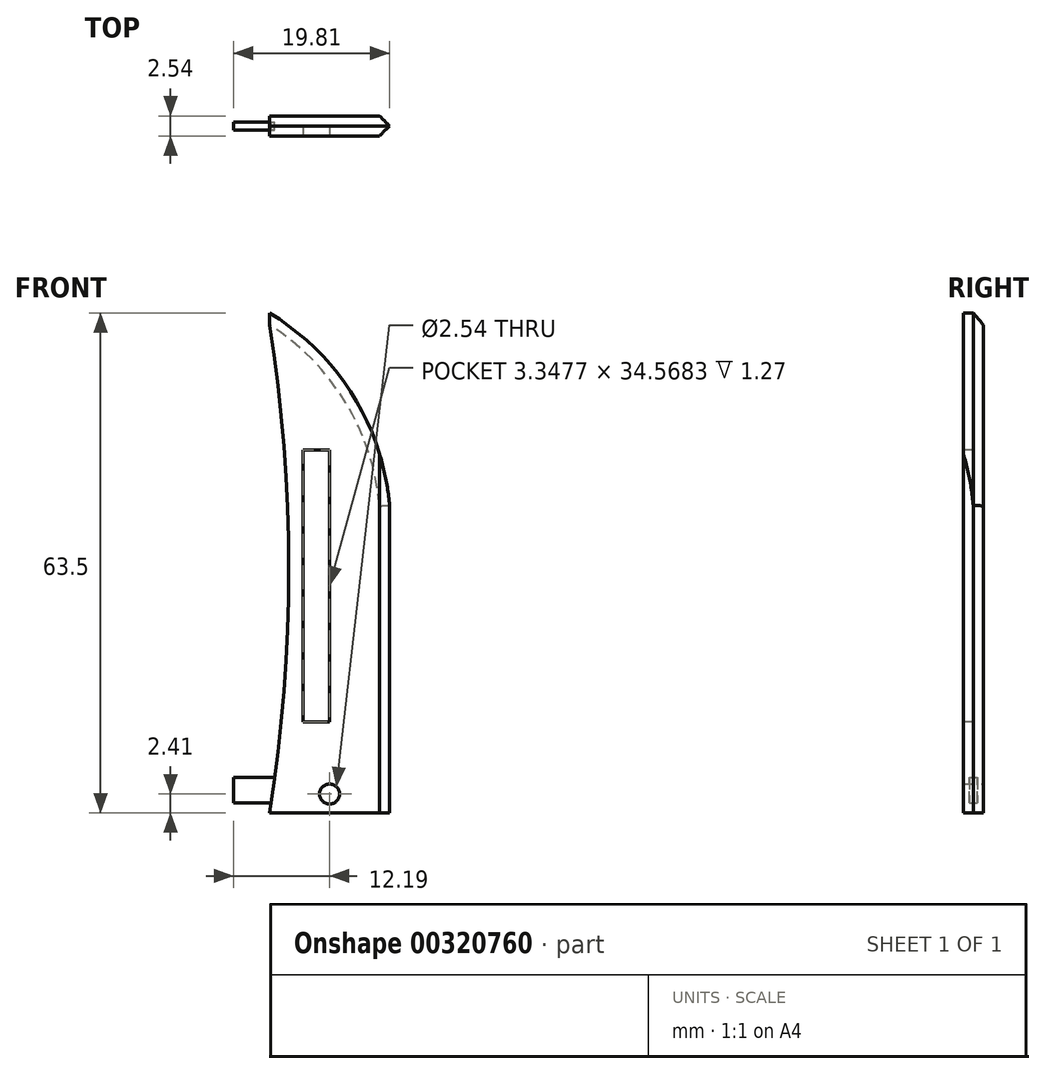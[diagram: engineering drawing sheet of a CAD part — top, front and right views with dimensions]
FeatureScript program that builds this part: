
annotation { "Feature Type Name" : "Feature", "Feature Type Description" : "" }
export const myFeature = defineFeature(function(context is Context, id is Id, definition is map)
    precondition{}
    {
        {
            var Q0;
            Q0=qCreatedBy(makeId("Front.planeOp"),FACE);
            var sketch = newSketch(context, id + "F0", { "sketchPlane" : qUnion([Q0])});
            skLineSegment(sketch, "E0", {"start": v(-7.62, 0) * mm, "end": v(-7.62, 63.5) * mm});
            skLineSegment(sketch, "E1", {"start": v(-7.62, 63.5) * mm, "end": v(7.62, 54.34) * mm});
            skLineSegment(sketch, "E2", {"start": v(7.62, 54.34) * mm, "end": v(7.62, 0) * mm});
            skLineSegment(sketch, "E3", {"start": v(7.62, 0) * mm, "end": v(-7.62, 0) * mm});
            skSolve(sketch);
        }
        {
            var Q0;
            Q0 = qSketchRegion(id + "F0", true);
            extrude(context, id + "F1", {"entities" : qUnion([Q0]), "endBound" : BoundingType.SYMMETRIC, "depth" : 2.54 * mm});
        }
        {
            var Q0;
            Q0=makeQuery(id+"F1.opExtrude","CAP_FACE",FACE,{"disambiguationData":[OSD([sQuery(id+"F0.wireOp",EDGE,"E0"),sQuery(id+"F0.wireOp",EDGE,"E1"),sQuery(id+"F0.wireOp",EDGE,"E2"),sQuery(id+"F0.wireOp",EDGE,"E3")])],"isStart":false});
            var sketch = newSketch(context, id + "F2", { "sketchPlane" : qUnion([Q0])});
            skArc(sketch, "E4", {"start": v(7.62, 39.07) * mm, "mid": v(2.94, 53.12) * mm, "end": v(-7.62, 63.5) * mm});
            skLineSegment(sketch, "E5", {"start": v(7.62, 39.07) * mm, "end": v(7.62, 63.5) * mm});
            skLineSegment(sketch, "E6", {"start": v(7.62, 63.5) * mm, "end": v(-7.62, 63.5) * mm});
            skSolve(sketch);
        }
        {
            var Q0;
            Q0 = qSketchRegion(id + "F2", true);
            extrude(context, id + "F3", {"entities" : qUnion([Q0]), "operationType" : NewBodyOperationType.REMOVE, "oppositeDirection" : true, "depth" : 25.4 * mm});
        }
        {
            var Q0;
            Q0=makeQuery(id+"F1.opExtrude","CAP_EDGE",EDGE,{"disambiguationData":[OSD([sQuery(id+"F0.wireOp",EDGE,"E2")])],"isStart":true});
            var Q1;
            Q1=makeQuery(id+"F3.boolean.opBoolean","INTERSECT",EDGE,{"derivedFrom":[makeQuery(id+"F1.opExtrude","CAP_FACE",FACE,{"disambiguationData":[OSD([sQuery(id+"F0.wireOp",EDGE,"E0"),sQuery(id+"F0.wireOp",EDGE,"E1"),sQuery(id+"F0.wireOp",EDGE,"E2"),sQuery(id+"F0.wireOp",EDGE,"E3")])],"isStart":true}),makeQuery(id+"F3.opExtrude","SWEPT_FACE",FACE,{"disambiguationData":[OSD([sQuery(id+"F2.wireOp",EDGE,"E4")])]})]});
            var Q2;
            Q2=makeQuery(id+"F1.opExtrude","CAP_EDGE",EDGE,{"disambiguationData":[OSD([sQuery(id+"F0.wireOp",EDGE,"E2")])],"isStart":false});
            var Q3;
            Q3=makeQuery(id+"F3.boolean.opBoolean","COPY",EDGE,{"derivedFrom":makeQuery(id+"F3.opExtrude","CAP_EDGE",EDGE,{"disambiguationData":[OSD([sQuery(id+"F2.wireOp",EDGE,"E4")])],"isStart":true})});
            chamfer(context, id + "F4", {"entities" : qUnion([Q0, Q1, Q2, Q3]), "width" : 1.27 * mm, "tangentPropagation" : true});
        }
        {
            var Q0;
            Q0=makeQuery(id+"F1.opExtrude","CAP_FACE",FACE,{"disambiguationData":[OSD([sQuery(id+"F0.wireOp",EDGE,"E0"),sQuery(id+"F0.wireOp",EDGE,"E1"),sQuery(id+"F0.wireOp",EDGE,"E2"),sQuery(id+"F0.wireOp",EDGE,"E3")])],"isStart":true});
            var sketch = newSketch(context, id + "F5", { "sketchPlane" : qUnion([Q0])});
            skArc(sketch, "E7", {"start": v(7.62, 62) * mm, "mid": v(5.19, 31) * mm, "end": v(7.62, 0) * mm});
            skLineSegment(sketch, "E8", {"start": v(7.62, 62) * mm, "end": v(7.62, 0) * mm});
            skSolve(sketch);
        }
        {
            var Q0;
            Q0 = qSketchRegion(id + "F5", true);
            extrude(context, id + "F6", {"entities" : qUnion([Q0]), "operationType" : NewBodyOperationType.REMOVE, "oppositeDirection" : true, "depth" : 25.4 * mm});
        }
        {
            var Q0;
            Q0=makeQuery(id+"F1.opExtrude","CAP_FACE",FACE,{"disambiguationData":[OSD([sQuery(id+"F0.wireOp",EDGE,"E0"),sQuery(id+"F0.wireOp",EDGE,"E1"),sQuery(id+"F0.wireOp",EDGE,"E2"),sQuery(id+"F0.wireOp",EDGE,"E3")])],"isStart":true});
            var sketch = newSketch(context, id + "F7", { "sketchPlane" : qUnion([Q0])});
            skCircle(sketch, "E9", {"center": v(0, 2.4) * mm, "radius": 1.27 * mm});
            skSolve(sketch);
        }
        {
            var Q0;
            Q0 = qSketchRegion(id + "F7", true);
            extrude(context, id + "F8", {"entities" : qUnion([Q0]), "operationType" : NewBodyOperationType.REMOVE, "oppositeDirection" : true, "depth" : 25.4 * mm});
        }
        {
            var Q0;
            Q0=makeQuery(id+"F1.opExtrude","CAP_FACE",FACE,{"disambiguationData":[OSD([sQuery(id+"F0.wireOp",EDGE,"E0"),sQuery(id+"F0.wireOp",EDGE,"E1"),sQuery(id+"F0.wireOp",EDGE,"E2"),sQuery(id+"F0.wireOp",EDGE,"E3")])],"isStart":false});
            var sketch = newSketch(context, id + "F9", { "sketchPlane" : qUnion([Q0])});
            skLineSegment(sketch, "E10.bottom", {"start": v(-3.35, 46.12) * mm, "end": v(0, 46.12) * mm});
            skLineSegment(sketch, "E10.top", {"start": v(-3.35, 11.55) * mm, "end": v(0, 11.55) * mm});
            skLineSegment(sketch, "E10.left", {"start": v(-3.35, 46.12) * mm, "end": v(-3.35, 11.55) * mm});
            skLineSegment(sketch, "E10.right", {"start": v(0, 46.12) * mm, "end": v(0, 11.55) * mm});
            skSolve(sketch);
        }
        {
            var Q0;
            Q0 = qSketchRegion(id + "F9", true);
            extrude(context, id + "F10", {"entities" : qUnion([Q0]), "operationType" : NewBodyOperationType.REMOVE, "oppositeDirection" : true, "depth" : 1.27 * mm});
        }
        {
            var Q0;
            Q0=makeQuery(id+"F10.boolean.opBoolean","COPY",FACE,{"derivedFrom":makeQuery(id+"F10.opExtrude","CAP_FACE",FACE,{"disambiguationData":[OSD([sQuery(id+"F9.wireOp",EDGE,"E10.bottom"),sQuery(id+"F9.wireOp",EDGE,"E10.top"),sQuery(id+"F9.wireOp",EDGE,"E10.left"),sQuery(id+"F9.wireOp",EDGE,"E10.right")])],"isStart":false})});
            var sketch = newSketch(context, id + "F11", { "sketchPlane" : qUnion([Q0])});
            skSolve(sketch);
        }
        {
            var Q0;
            Q0=makeQuery(id+"F11.imprint","IMPRINT",FACE,{"disambiguationData":[TD([[makeQuery(id+"F11.imprint","IMPRINT",EDGE,{"derivedFrom":makeQuery(id+"F10.boolean.opBoolean","COPY",EDGE,{"derivedFrom":makeQuery(id+"F10.opExtrude","CAP_EDGE",EDGE,{"disambiguationData":[OSD([sQuery(id+"F9.wireOp",EDGE,"E10.bottom")])],"isStart":false})})}),-1.0]])]});
            extrude(context, id + "F12", {"entities" : qUnion([Q0]), "depth" : 1.27 * mm});
        }
        {
            var Q0;
            Q0 = qSketchRegion(id + "F9", true);
            extrude(context, id + "F13", {"entities" : qUnion([Q0]), "operationType" : NewBodyOperationType.REMOVE, "oppositeDirection" : true, "depth" : 1.27 * mm});
        }
        {
            var Q0;
            Q0=qCreatedBy(makeId("Right.planeOp"),FACE);
            var sketch = newSketch(context, id + "F14", { "sketchPlane" : qUnion([Q0])});
            skLineSegment(sketch, "E11", {"start": v(0.5, 1.25) * mm, "end": v(-0.5, 1.25) * mm});
            skLineSegment(sketch, "E12", {"start": v(-0.5, 1.25) * mm, "end": v(-0.5, 4.51) * mm});
            skLineSegment(sketch, "E13", {"start": v(-0.5, 4.51) * mm, "end": v(0.5, 4.51) * mm});
            skLineSegment(sketch, "E14", {"start": v(0.5, 4.51) * mm, "end": v(0.5, 1.25) * mm});
            skSolve(sketch);
        }
        {
            var Q0;
            Q0 = qSketchRegion(id + "F14", true);
            extrude(context, id + "F15", {"entities" : qUnion([Q0]), "operationType" : NewBodyOperationType.ADD, "oppositeDirection" : true, "depth" : 12.2 * mm});
        }
        {
            var Q0;
            Q0=qCreatedBy(makeId("Front.planeOp"),FACE);
            var sketch = newSketch(context, id + "F16", { "sketchPlane" : qUnion([Q0])});
            skCircle(sketch, "E15.0", {"center": v(0, 2.4) * mm, "radius": 1.27 * mm});
            skSolve(sketch);
        }
        {
            var Q0;
            Q0 = qSketchRegion(id + "F16", true);
            extrude(context, id + "F17", {"entities" : qUnion([Q0]), "operationType" : NewBodyOperationType.REMOVE, "endBound" : BoundingType.SYMMETRIC, "oppositeDirection" : true, "depth" : 25.4 * mm});
        }
    });
